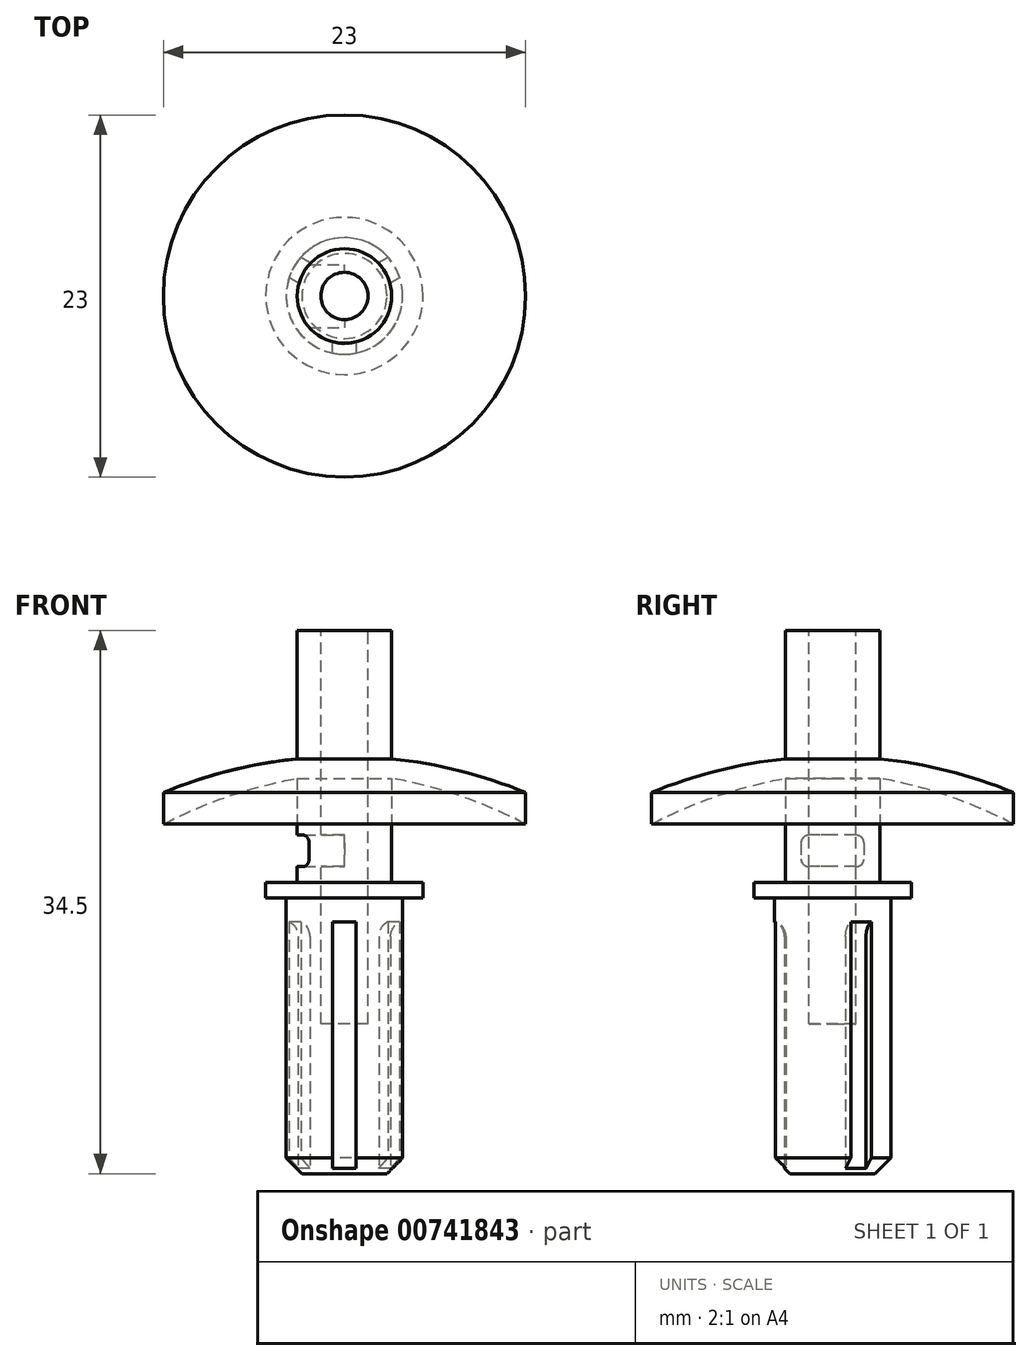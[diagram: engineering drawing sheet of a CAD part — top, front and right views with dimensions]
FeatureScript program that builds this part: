
annotation { "Feature Type Name" : "Feature", "Feature Type Description" : "" }
export const myFeature = defineFeature(function(context is Context, id is Id, definition is map)
    precondition{}
    {
        {
            var Q0;
            Q0=qCreatedBy(makeId("Top.planeOp"),FACE);
            var sketch = newSketch(context, id + "F0", { "sketchPlane" : qUnion([Q0])});
            skCircle(sketch, "E0", {"center": v(0, 0) * mm, "radius": 3.7 * mm});
            skSolve(sketch);
        }
        {
            var Q0;
            Q0=makeQuery(id+"F0.imprint","IMPRINT",FACE,{"disambiguationData":[TD([[makeQuery(id+"F0.imprint","IMPRINT",EDGE,{"derivedFrom":sQuery(id+"F0.wireOp",EDGE,"E0")}),1.0]])]});
            extrude(context, id + "F1", {"entities" : qUnion([Q0]), "oppositeDirection" : true, "depth" : 17.5 * mm, "offsetDistance" : 25 * mm});
        }
        {
            var Q0;
            Q0=makeQuery(id+"F1.opExtrude","CAP_FACE",FACE,{"disambiguationData":[OSD([sQuery(id+"F0.wireOp",EDGE,"E0")])],"isStart":false});
            var sketch = newSketch(context, id + "F2", { "sketchPlane" : qUnion([Q0])});
            skArc(sketch, "E1", {"start": v(-2.94, -0.83) * mm, "mid": v(-2.64, -1.52) * mm, "end": v(-2.19, -2.13) * mm});
            skLineSegment(sketch, "E2", {"start": v(-0.75, 2.96) * mm, "end": v(-0.75, 3.62) * mm});
            skLineSegment(sketch, "E3", {"start": v(0.75, 2.96) * mm, "end": v(0.75, 3.62) * mm});
            skArc(sketch, "E4", {"start": v(0.75, 3.62) * mm, "mid": v(0, 3.7) * mm, "end": v(-0.75, 3.62) * mm});
            skArc(sketch, "E5.1.0", {"start": v(-3.51, -1.16) * mm, "mid": v(-3.2, -1.85) * mm, "end": v(-2.76, -2.46) * mm});
            skArc(sketch, "E5.2.0", {"start": v(2.76, -2.46) * mm, "mid": v(3.2, -1.85) * mm, "end": v(3.51, -1.16) * mm});
            skLineSegment(sketch, "E6.1.0", {"start": v(-2.94, -0.83) * mm, "end": v(-3.51, -1.16) * mm});
            skLineSegment(sketch, "E6.1.1", {"start": v(-2.19, -2.13) * mm, "end": v(-2.76, -2.46) * mm});
            skLineSegment(sketch, "E6.2.0", {"start": v(2.19, -2.13) * mm, "end": v(2.76, -2.46) * mm});
            skLineSegment(sketch, "E6.2.1", {"start": v(2.94, -0.83) * mm, "end": v(3.51, -1.16) * mm});
            skArc(sketch, "E7.trimOffspring", {"start": v(0.75, 2.96) * mm, "mid": v(0, 3.05) * mm, "end": v(-0.75, 2.96) * mm});
            skArc(sketch, "E8.trimOffspring", {"start": v(2.19, -2.13) * mm, "mid": v(2.64, -1.52) * mm, "end": v(2.94, -0.83) * mm});
            skSolve(sketch);
        }
        {
            var Q0;
            Q0 = qSketchRegion(id + "F2", true);
            extrude(context, id + "F3", {"entities" : qUnion([Q0]), "operationType" : NewBodyOperationType.REMOVE, "oppositeDirection" : true, "depth" : 16 * mm, "offsetDistance" : 25 * mm});
        }
        {
            var Q0;
            Q0=makeQuery(id+"F3.boolean.opBoolean","COPY",EDGE,{"derivedFrom":makeQuery(id+"F3.opExtrude","CAP_EDGE",EDGE,{"disambiguationData":[OSD([sQuery(id+"F2.wireOp",EDGE,"E8.trimOffspring")])],"isStart":false})});
            var Q1;
            Q1=makeQuery(id+"F3.boolean.opBoolean","COPY",EDGE,{"derivedFrom":makeQuery(id+"F3.opExtrude","CAP_EDGE",EDGE,{"disambiguationData":[OSD([sQuery(id+"F2.wireOp",EDGE,"E7.trimOffspring")])],"isStart":false})});
            var Q2;
            Q2=makeQuery(id+"F3.boolean.opBoolean","COPY",EDGE,{"derivedFrom":makeQuery(id+"F3.opExtrude","CAP_EDGE",EDGE,{"disambiguationData":[OSD([sQuery(id+"F2.wireOp",EDGE,"E1")])],"isStart":false})});
            fillet(context, id + "F4", {"entities" : qUnion([Q0, Q1, Q2]), "radius" : 1 * mm, "tangentPropagation" : true, "allowEdgeOverflow" : false});
        }
        {
            var Q0;
            {var subQ0=sQuery(id+"F0.wireOp",EDGE,"E0");Q0=makeQuery(id+"F3.boolean.opBoolean","SPLIT",EDGE,{"disambiguationData":[TD([makeQuery(id+"F3.opExtrude","SWEPT_FACE",FACE,{"disambiguationData":[OSD([sQuery(id+"F2.wireOp",EDGE,"E2")])]})])],"derivedFrom":makeQuery(id+"F1.opExtrude","CAP_EDGE",EDGE,{"disambiguationData":[OSD([subQ0])],"isStart":false})});}
            chamfer(context, id + "F5", {"entities" : qUnion([Q0]), "width" : 1 * mm, "tangentPropagation" : true});
        }
        {
            var Q0;
            Q0=makeQuery(id+"F1.opExtrude","CAP_FACE",FACE,{"disambiguationData":[OSD([sQuery(id+"F0.wireOp",EDGE,"E0")])],"isStart":true});
            var sketch = newSketch(context, id + "F6", { "sketchPlane" : qUnion([Q0])});
            skCircle(sketch, "E9", {"center": v(0, 0) * mm, "radius": 5 * mm});
            skSolve(sketch);
        }
        {
            var Q0;
            Q0 = qSketchRegion(id + "F6", true);
            extrude(context, id + "F7", {"entities" : qUnion([Q0]), "operationType" : NewBodyOperationType.ADD, "depth" : 1 * mm, "offsetDistance" : 25 * mm});
        }
        {
            var Q0;
            Q0=makeQuery(id+"F7.opExtrude","CAP_FACE",FACE,{"disambiguationData":[OSD([sQuery(id+"F6.wireOp",EDGE,"E9")])],"isStart":false});
            var sketch = newSketch(context, id + "F8", { "sketchPlane" : qUnion([Q0])});
            skCircle(sketch, "E10", {"center": v(0, 0) * mm, "radius": 3 * mm});
            skSolve(sketch);
        }
        {
            var Q0;
            Q0 = qSketchRegion(id + "F8", true);
            extrude(context, id + "F9", {"entities" : qUnion([Q0]), "operationType" : NewBodyOperationType.ADD, "depth" : 16 * mm, "offsetDistance" : 25 * mm});
        }
        {
            var Q0;
            Q0=qCreatedBy(makeId("Right.planeOp"),FACE);
            var sketch = newSketch(context, id + "F10", { "sketchPlane" : qUnion([Q0])});
            skArc(sketch, "E11", {"start": v(0, 9) * mm, "mid": v(-5.86, 8.42) * mm, "end": v(-11.5, 6.7) * mm});
            skLineSegment(sketch, "E12", {"start": v(-11.5, 6.7) * mm, "end": v(-11.5, 4.7) * mm});
            skLineSegment(sketch, "E13", {"start": v(0, 9) * mm, "end": v(0, 8) * mm});
            skArc(sketch, "E14", {"start": v(0, 8) * mm, "mid": v(-5.92, 6.93) * mm, "end": v(-11.5, 4.7) * mm});
            skSolve(sketch);
        }
        {
            var Q0;
            Q0=qCreatedBy(makeId("Front.planeOp"),FACE);
            var sketch = newSketch(context, id + "F11", { "sketchPlane" : qUnion([Q0])});
            skLineSegment(sketch, "E15", {"start": v(0, 0) * mm, "end": v(0, 16.4) * mm, "construction": true});
            skSolve(sketch);
        }
        {
            var Q0;
            Q0=makeQuery(id+"F10.imprint","IMPRINT",FACE,{"disambiguationData":[TD([[makeQuery(id+"F10.imprint","IMPRINT",EDGE,{"derivedFrom":sQuery(id+"F10.wireOp",EDGE,"E11")}),1.0]])]});
            var Q1;
            Q1=sQuery(id+"F11.wireOp",EDGE,"E15");
            revolve(context, id + "F12", {"operationType" : NewBodyOperationType.ADD, "surfaceOperationType" : NewSurfaceOperationType.NEW, "entities" : qUnion([Q0]), "axis" : qUnion([Q1]), "revolveType" : RevolveType.FULL});
        }
        {
            var Q0;
            Q0=qCreatedBy(makeId("Right.planeOp"),FACE);
            var sketch = newSketch(context, id + "F13", { "sketchPlane" : qUnion([Q0])});
            skLineSegment(sketch, "E16.bottom", {"start": v(1.5, 4) * mm, "end": v(-1.5, 4) * mm});
            skLineSegment(sketch, "E16.top", {"start": v(1.5, 2) * mm, "end": v(-1.5, 2) * mm});
            skLineSegment(sketch, "E16.left", {"start": v(2, 3.5) * mm, "end": v(2, 2.5) * mm});
            skLineSegment(sketch, "E16.right", {"start": v(-2, 3.5) * mm, "end": v(-2, 2.5) * mm});
            skPoint(sketch, "E17.visualSharp", {"position": v(2, 4) * mm});
            skArc(sketch, "E17.filletArc", {"start": v(2, 3.5) * mm, "mid": v(1.85, 3.85) * mm, "end": v(1.5, 4) * mm});
            skPoint(sketch, "E18.visualSharp", {"position": v(2, 2) * mm});
            skArc(sketch, "E18.filletArc", {"start": v(1.5, 2) * mm, "mid": v(1.85, 2.15) * mm, "end": v(2, 2.5) * mm});
            skPoint(sketch, "E19.visualSharp", {"position": v(-2, 2) * mm});
            skArc(sketch, "E19.filletArc", {"start": v(-2, 2.5) * mm, "mid": v(-1.85, 2.15) * mm, "end": v(-1.5, 2) * mm});
            skPoint(sketch, "E20.visualSharp", {"position": v(-2, 4) * mm});
            skArc(sketch, "E20.filletArc", {"start": v(-1.5, 4) * mm, "mid": v(-1.85, 3.85) * mm, "end": v(-2, 3.5) * mm});
            skSolve(sketch);
        }
        {
            var Q0;
            Q0 = qSketchRegion(id + "F13", true);
            extrude(context, id + "F14", {"entities" : qUnion([Q0]), "operationType" : NewBodyOperationType.REMOVE, "oppositeDirection" : true, "depth" : 25 * mm, "offsetDistance" : 25 * mm});
        }
        {
            var Q0;
            Q0=makeQuery(id+"F9.opExtrude","CAP_FACE",FACE,{"disambiguationData":[OSD([sQuery(id+"F8.wireOp",EDGE,"E10")])],"isStart":false});
            var sketch = newSketch(context, id + "F15", { "sketchPlane" : qUnion([Q0])});
            skCircle(sketch, "E21", {"center": v(0, 0) * mm, "radius": 1.5 * mm});
            skSolve(sketch);
        }
        {
            var Q0;
            Q0=makeQuery(id+"F15.imprint","IMPRINT",FACE,{"disambiguationData":[TD([[makeQuery(id+"F15.imprint","IMPRINT",EDGE,{"derivedFrom":sQuery(id+"F15.wireOp",EDGE,"E21")}),1.0]])]});
            var Q1;
            Q1=sQuery(id+"F15.wireOp",EDGE,"E21");
            extrude(context, id + "F16", {"entities" : qUnion([Q0]), "operationType" : NewBodyOperationType.REMOVE, "surfaceEntities" : qUnion([Q1]), "oppositeDirection" : true, "depth" : 25 * mm, "offsetDistance" : 25 * mm});
        }
    });
